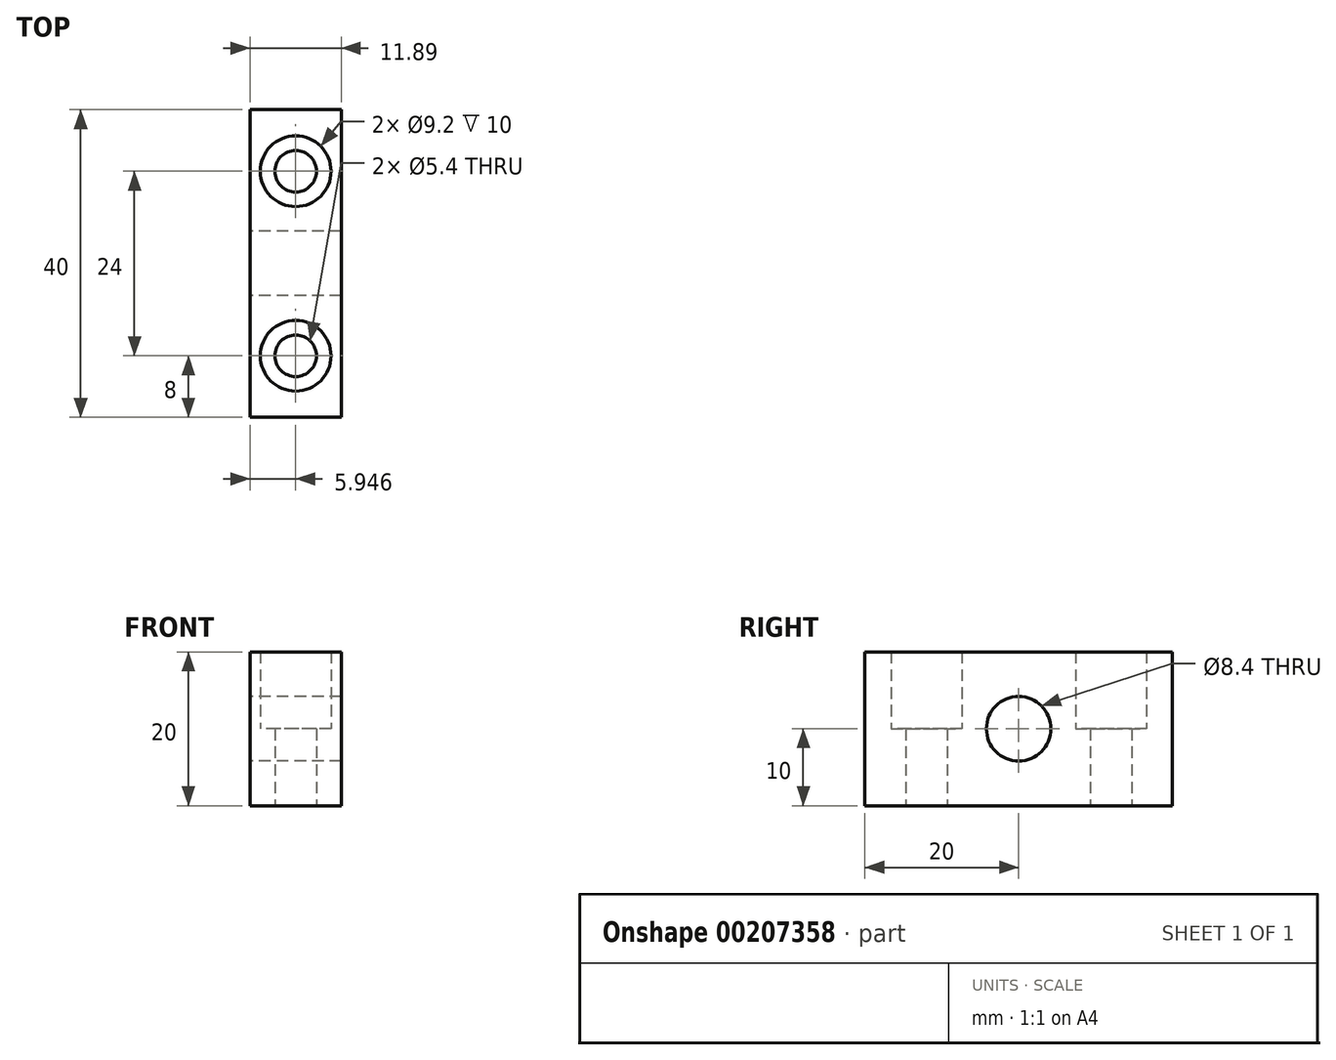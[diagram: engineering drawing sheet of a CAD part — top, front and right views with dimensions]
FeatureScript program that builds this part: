
annotation { "Feature Type Name" : "Feature", "Feature Type Description" : "" }
export const myFeature = defineFeature(function(context is Context, id is Id, definition is map)
    precondition{}
    {
        {
            var Q0;
            Q0=qCreatedBy(makeId("Top.planeOp"),FACE);
            var sketch = newSketch(context, id + "F0", { "sketchPlane" : qUnion([Q0])});
            skLineSegment(sketch, "E0.bottom", {"start": v(0, 0) * mm, "end": v(-11.89, 0) * mm});
            skLineSegment(sketch, "E0.top", {"start": v(0, -40) * mm, "end": v(-11.89, -40) * mm});
            skLineSegment(sketch, "E0.left", {"start": v(0, 0) * mm, "end": v(0, -40) * mm});
            skLineSegment(sketch, "E0.right", {"start": v(-11.89, 0) * mm, "end": v(-11.89, -40) * mm});
            skCircle(sketch, "E1", {"center": v(-5.94, -8) * mm, "radius": 2.7 * mm});
            skCircle(sketch, "E2", {"center": v(-5.94, -32) * mm, "radius": 2.7 * mm});
            skPoint(sketch, "E3", {"position": v(-5.94, 0) * mm});
            skCircle(sketch, "E4", {"center": v(-5.94, -8) * mm, "radius": 4.6 * mm});
            skCircle(sketch, "E5", {"center": v(-5.94, -32) * mm, "radius": 4.6 * mm});
            skSolve(sketch);
        }
        {
            var Q0;
            Q0=makeQuery(id+"F0.imprint","IMPRINT",FACE,{"disambiguationData":[TD([[makeQuery(id+"F0.imprint","IMPRINT",EDGE,{"derivedFrom":sQuery(id+"F0.wireOp",EDGE,"E0.bottom")}),1.0]])]});
            extrude(context, id + "F1", {"entities" : qUnion([Q0]), "depth" : 20 * mm});
        }
        {
            var Q0;
            Q0=makeQuery(id+"F0.imprint","IMPRINT",FACE,{"disambiguationData":[TD([[makeQuery(id+"F0.imprint","IMPRINT",EDGE,{"derivedFrom":sQuery(id+"F0.wireOp",EDGE,"E1")}),-1.0]])]});
            var Q1;
            Q1=makeQuery(id+"F0.imprint","IMPRINT",FACE,{"disambiguationData":[TD([[makeQuery(id+"F0.imprint","IMPRINT",EDGE,{"derivedFrom":sQuery(id+"F0.wireOp",EDGE,"E2")}),-1.0]])]});
            extrude(context, id + "F2", {"entities" : qUnion([Q0, Q1]), "operationType" : NewBodyOperationType.ADD, "depth" : 10 * mm});
        }
        {
            var Q0;
            Q0=makeQuery(id+"F1.opExtrude","SWEPT_FACE",FACE,{"disambiguationData":[OSD([sQuery(id+"F0.wireOp",EDGE,"E0.right")])]});
            var sketch = newSketch(context, id + "F3", { "sketchPlane" : qUnion([Q0])});
            skPoint(sketch, "E6", {"position": v(20, 0) * mm});
            skCircle(sketch, "E7", {"center": v(20, 10) * mm, "radius": 4.2 * mm});
            skSolve(sketch);
        }
        {
            var Q0;
            Q0=makeQuery(id+"F3.imprint","IMPRINT",FACE,{"disambiguationData":[TD([[makeQuery(id+"F3.imprint","IMPRINT",EDGE,{"derivedFrom":sQuery(id+"F3.wireOp",EDGE,"E7")}),1.0]])]});
            var Q1;
            Q1=makeQuery(id+"F1.opExtrude","SWEPT_FACE",FACE,{"disambiguationData":[OSD([sQuery(id+"F0.wireOp",EDGE,"E0.left")])]});
            extrude(context, id + "F4", {"entities" : qUnion([Q0]), "operationType" : NewBodyOperationType.REMOVE, "endBound" : BoundingType.UP_TO_SURFACE, "oppositeDirection" : true, "endBoundEntityFace" : qUnion([Q1]), "depth" : 25 * mm});
        }
    });
